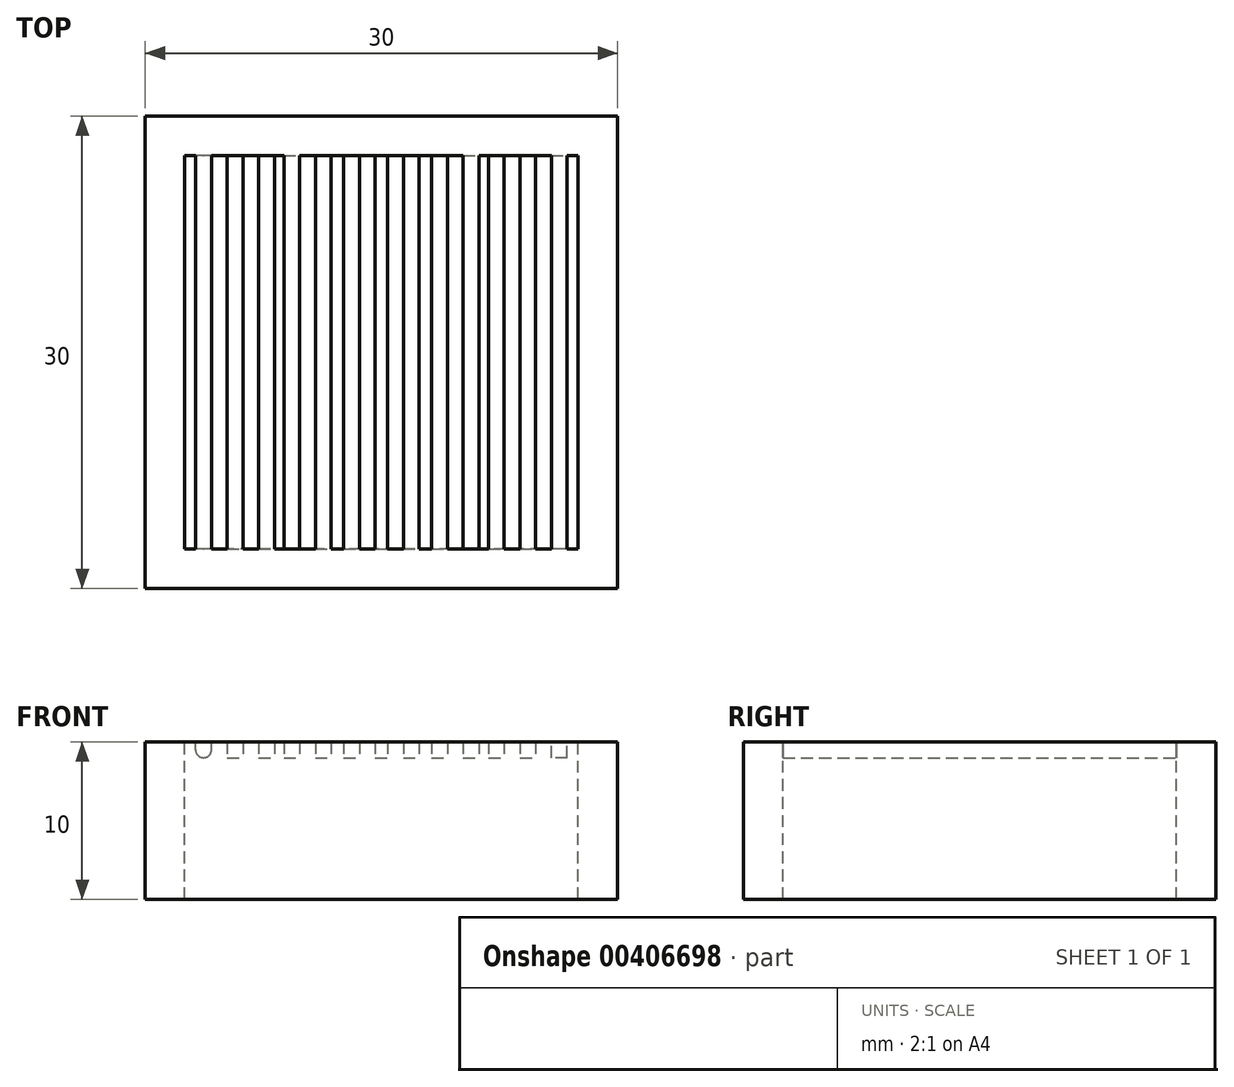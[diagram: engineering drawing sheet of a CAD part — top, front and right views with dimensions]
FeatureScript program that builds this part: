
annotation { "Feature Type Name" : "Feature", "Feature Type Description" : "" }
export const myFeature = defineFeature(function(context is Context, id is Id, definition is map)
    precondition{}
    {
        {
            var Q0;
            Q0=qCreatedBy(makeId("Top.planeOp"),FACE);
            var sketch = newSketch(context, id + "F0", { "sketchPlane" : qUnion([Q0])});
            skLineSegment(sketch, "E0.bottom", {"start": v(15, -15) * mm, "end": v(-15, -15) * mm});
            skLineSegment(sketch, "E0.top", {"start": v(15, 15) * mm, "end": v(-15, 15) * mm});
            skLineSegment(sketch, "E0.left", {"start": v(15, -15) * mm, "end": v(15, 15) * mm});
            skLineSegment(sketch, "E0.right", {"start": v(-15, -15) * mm, "end": v(-15, 15) * mm});
            skPoint(sketch, "E0.middle", {"position": v(0, 0) * mm});
            skLineSegment(sketch, "E1.bottom", {"start": v(12.5, -12.5) * mm, "end": v(-12.5, -12.5) * mm});
            skLineSegment(sketch, "E1.top", {"start": v(12.5, 12.5) * mm, "end": v(-12.5, 12.5) * mm});
            skLineSegment(sketch, "E1.left", {"start": v(12.5, -12.5) * mm, "end": v(12.5, 12.5) * mm});
            skLineSegment(sketch, "E1.right", {"start": v(-12.5, -12.5) * mm, "end": v(-12.5, 12.5) * mm});
            skSolve(sketch);
        }
        {
            var Q0;
            Q0 = qSketchRegion(id + "F0", true);
            extrude(context, id + "F1", {"entities" : qUnion([Q0]), "oppositeDirection" : true, "depth" : 10 * mm});
        }
        {
            var Q0;
            Q0=qCreatedBy(makeId("Top.planeOp"),FACE);
            var sketch = newSketch(context, id + "F2", { "sketchPlane" : qUnion([Q0])});
            skLineSegment(sketch, "E2.bottom", {"start": v(-11.8, -12.5) * mm, "end": v(-10.8, -12.5) * mm});
            skLineSegment(sketch, "E2.top", {"start": v(-11.8, 12.5) * mm, "end": v(-10.8, 12.5) * mm});
            skLineSegment(sketch, "E2.left", {"start": v(-11.8, -12.5) * mm, "end": v(-11.8, 12.5) * mm});
            skLineSegment(sketch, "E2.right", {"start": v(-10.8, -12.5) * mm, "end": v(-10.8, 12.5) * mm});
            skLineSegment(sketch, "E3.MirrorCS", {"start": v(11.8, -12.5) * mm, "end": v(11.8, 12.5) * mm});
            skLineSegment(sketch, "E4.MirrorCS", {"start": v(10.8, -12.5) * mm, "end": v(10.8, 12.5) * mm});
            skLineSegment(sketch, "E5.MirrorCS", {"start": v(11.8, 12.5) * mm, "end": v(10.8, 12.5) * mm});
            skLineSegment(sketch, "E6.MirrorCS", {"start": v(11.8, -12.5) * mm, "end": v(10.8, -12.5) * mm});
            skLineSegment(sketch, "E7.bottom", {"start": v(-9.8, -12.52) * mm, "end": v(-8.8, -12.52) * mm});
            skLineSegment(sketch, "E7.top", {"start": v(-9.8, 12.48) * mm, "end": v(-8.8, 12.48) * mm});
            skLineSegment(sketch, "E7.left", {"start": v(-9.8, -12.52) * mm, "end": v(-9.8, 12.48) * mm});
            skLineSegment(sketch, "E7.right", {"start": v(-8.8, -12.52) * mm, "end": v(-8.8, 12.48) * mm});
            skLineSegment(sketch, "E8.MirrorCS", {"start": v(-9.8, -12.52) * mm, "end": v(-10.8, -12.52) * mm});
            skLineSegment(sketch, "E9.MirrorCS", {"start": v(8.8, -12.52) * mm, "end": v(8.8, 12.48) * mm});
            skLineSegment(sketch, "E10.MirrorCS", {"start": v(9.8, -12.52) * mm, "end": v(9.8, 12.48) * mm});
            skLineSegment(sketch, "E11.MirrorCS", {"start": v(9.8, -12.52) * mm, "end": v(8.8, -12.52) * mm});
            skLineSegment(sketch, "E12.MirrorCS", {"start": v(9.8, 12.48) * mm, "end": v(8.8, 12.48) * mm});
            skLineSegment(sketch, "E13.bottom", {"start": v(-7.8, -12.52) * mm, "end": v(-6.8, -12.52) * mm});
            skLineSegment(sketch, "E13.top", {"start": v(-7.8, 12.48) * mm, "end": v(-6.8, 12.48) * mm});
            skLineSegment(sketch, "E13.left", {"start": v(-7.8, -12.52) * mm, "end": v(-7.8, 12.48) * mm});
            skLineSegment(sketch, "E13.right", {"start": v(-6.8, -12.52) * mm, "end": v(-6.8, 12.48) * mm});
            skLineSegment(sketch, "E14.MirrorCS", {"start": v(7.8, -12.52) * mm, "end": v(7.8, 12.48) * mm});
            skLineSegment(sketch, "E15.MirrorCS", {"start": v(7.8, -12.52) * mm, "end": v(6.8, -12.52) * mm});
            skLineSegment(sketch, "E16.MirrorCS", {"start": v(6.8, -12.52) * mm, "end": v(6.8, 12.48) * mm});
            skLineSegment(sketch, "E17.MirrorCS", {"start": v(7.8, 12.48) * mm, "end": v(6.8, 12.48) * mm});
            skLineSegment(sketch, "E18.bottom", {"start": v(-6.2, -12.48) * mm, "end": v(-5.2, -12.48) * mm});
            skLineSegment(sketch, "E18.top", {"start": v(-6.2, 12.52) * mm, "end": v(-5.2, 12.52) * mm});
            skLineSegment(sketch, "E18.left", {"start": v(-6.2, -12.48) * mm, "end": v(-6.2, 12.52) * mm});
            skLineSegment(sketch, "E18.right", {"start": v(-5.2, -12.48) * mm, "end": v(-5.2, 12.52) * mm});
            skLineSegment(sketch, "E19.bottom", {"start": v(-4.2, -12.52) * mm, "end": v(-3.2, -12.52) * mm});
            skLineSegment(sketch, "E19.top", {"start": v(-4.2, 12.48) * mm, "end": v(-3.2, 12.48) * mm});
            skLineSegment(sketch, "E19.left", {"start": v(-4.2, -12.52) * mm, "end": v(-4.2, 12.48) * mm});
            skLineSegment(sketch, "E19.right", {"start": v(-3.2, -12.52) * mm, "end": v(-3.2, 12.48) * mm});
            skLineSegment(sketch, "E20.bottom", {"start": v(-2.4, -12.52) * mm, "end": v(-1.4, -12.52) * mm});
            skLineSegment(sketch, "E20.top", {"start": v(-2.4, 12.48) * mm, "end": v(-1.4, 12.48) * mm});
            skLineSegment(sketch, "E20.left", {"start": v(-2.4, -12.52) * mm, "end": v(-2.4, 12.48) * mm});
            skLineSegment(sketch, "E20.right", {"start": v(-1.4, -12.52) * mm, "end": v(-1.4, 12.48) * mm});
            skLineSegment(sketch, "E21.bottom", {"start": v(-0.4, -12.52) * mm, "end": v(0.4, -12.52) * mm});
            skLineSegment(sketch, "E21.top", {"start": v(-0.4, 12.48) * mm, "end": v(0.4, 12.48) * mm});
            skLineSegment(sketch, "E21.left", {"start": v(-0.4, -12.52) * mm, "end": v(-0.4, 12.48) * mm});
            skLineSegment(sketch, "E21.right", {"start": v(0.4, -12.52) * mm, "end": v(0.4, 12.48) * mm});
            skLineSegment(sketch, "E22.MirrorCS", {"start": v(-6.2, -12.48) * mm, "end": v(-7.2, -12.48) * mm});
            skLineSegment(sketch, "E23.MirrorCS", {"start": v(6.2, -12.48) * mm, "end": v(6.2, 12.52) * mm});
            skLineSegment(sketch, "E24.MirrorCS", {"start": v(6.2, -12.48) * mm, "end": v(5.2, -12.48) * mm});
            skLineSegment(sketch, "E25.MirrorCS", {"start": v(5.2, -12.48) * mm, "end": v(5.2, 12.52) * mm});
            skLineSegment(sketch, "E26.MirrorCS", {"start": v(6.2, 12.52) * mm, "end": v(5.2, 12.52) * mm});
            skLineSegment(sketch, "E27.MirrorCS", {"start": v(4.2, -12.52) * mm, "end": v(4.2, 12.48) * mm});
            skLineSegment(sketch, "E28.MirrorCS", {"start": v(4.2, 12.48) * mm, "end": v(3.2, 12.48) * mm});
            skLineSegment(sketch, "E29.MirrorCS", {"start": v(3.2, -12.52) * mm, "end": v(3.2, 12.48) * mm});
            skLineSegment(sketch, "E30.MirrorCS", {"start": v(4.2, -12.52) * mm, "end": v(3.2, -12.52) * mm});
            skLineSegment(sketch, "E31.MirrorCS", {"start": v(2.4, -12.52) * mm, "end": v(1.4, -12.52) * mm});
            skLineSegment(sketch, "E32.MirrorCS", {"start": v(2.4, -12.52) * mm, "end": v(2.4, 12.48) * mm});
            skLineSegment(sketch, "E33.MirrorCS", {"start": v(1.4, -12.52) * mm, "end": v(1.4, 12.48) * mm});
            skLineSegment(sketch, "E34.MirrorCS", {"start": v(2.4, 12.48) * mm, "end": v(1.4, 12.48) * mm});
            skSolve(sketch);
        }
        {
            var Q0;
            Q0 = qSketchRegion(id + "F2", true);
            extrude(context, id + "F3", {"entities" : qUnion([Q0]), "operationType" : NewBodyOperationType.ADD, "oppositeDirection" : true, "depth" : 1 * mm});
        }
        {
            var Q0;
            Q0=makeQuery(id+"F3.opExtrude","CAP_EDGE",EDGE,{"disambiguationData":[OSD([sQuery(id+"F2.wireOp",EDGE,"E2.left")])],"isStart":false});
            fillet(context, id + "F4", {"entities" : qUnion([Q0]), "radius" : 0.48 * mm, "tangentPropagation" : true, "allowEdgeOverflow" : false});
        }
        {
            var Q0;
            {var subQ0=sQuery(id+"F2.wireOp",EDGE,"E2.left");Q0=makeQuery(id+"F4.opFillet","BLEND_EDGE",EDGE,{"blendedFrom":[makeQuery(id+"F3.opExtrude","CAP_EDGE",EDGE,{"disambiguationData":[OSD([subQ0])],"isStart":false}),makeQuery(id+"F3.opExtrude","CAP_FACE",FACE,{"disambiguationData":[OSD([sQuery(id+"F2.wireOp",EDGE,"E2.bottom"),sQuery(id+"F2.wireOp",EDGE,"E2.top"),subQ0,sQuery(id+"F2.wireOp",EDGE,"E2.right")])],"isStart":false})],"blendedInto":[makeQuery(id+"F3.opExtrude","CAP_FACE",FACE,{"disambiguationData":[OSD([sQuery(id+"F2.wireOp",EDGE,"E2.bottom"),sQuery(id+"F2.wireOp",EDGE,"E2.top"),subQ0,sQuery(id+"F2.wireOp",EDGE,"E2.right")])],"isStart":false})]});}
            var Q1;
            Q1=makeQuery(id+"F3.opExtrude","CAP_EDGE",EDGE,{"disambiguationData":[OSD([sQuery(id+"F2.wireOp",EDGE,"E2.right")])],"isStart":false});
            fillet(context, id + "F5", {"entities" : qUnion([Q0, Q1]), "radius" : 0.48 * mm, "tangentPropagation" : true, "allowEdgeOverflow" : false});
        }
    });
